# Revit family: Plumbing-Fix_Soap-Container_Stern_Bottle
name_source: partatom
category: Plumbing Fixtures
units: mm (PartAtom-declared; Revit-internal decimal feet)

## family parameters
Always vertical = No
Classification Number = 23.45.05.00
Cut with Voids When Loaded = No
Enable Cutting in Views = No
Maintain Annotation Orientation = No
Part Type = Normal
Room Calculation Point = No
Round Connector Dimension = Use Diameter
Shared = No
Work Plane-Based = Yes

## types (2) — shared parameters
Assembly Code = D2090900
CW Connection = No
Capacity = 33 oz / 1 liter
Default Elevation = 0' - 0"
HW Connection = No
Manufacturer = Stern Engineering
Manufacturer Website = http://www.sternfaucets.com
Model = Soap Bottle
Product Data = http://www.arcat.com
Revision = R1_2018-04
Sales Information = http://www.sternfaucets.com
Type Comments = Max. Distance between pump and MF tank: 3 meters / 9.8 feet
URL = http://www.sternfaucets.com
Unit Depth = 0' - 5"
Unit Height = 1' - 0 7/8"
Unit Width = 0' - 3 5/8"
Vent Connection = No
Warranty Duration (Years) = 2
Waste Connection = No
zero-valued in all types: CWFU, Cost, Expected Lifespan (Years), HWFU, Maintenance Schedule (Months), WFU

## per-type parameters (varying)
| type | Description | Include Pump on Bottle |
| Single Feed | Stern Single Feed Soap Container - 33 oz / 1 liter | Yes |
| Multifeed | Stern Multifeed Soap Container - 33 oz / 1 liter | No |

## geometry (parser evidence)
native form markers: Sweep x8
no freeform markers — native parametric forms only
